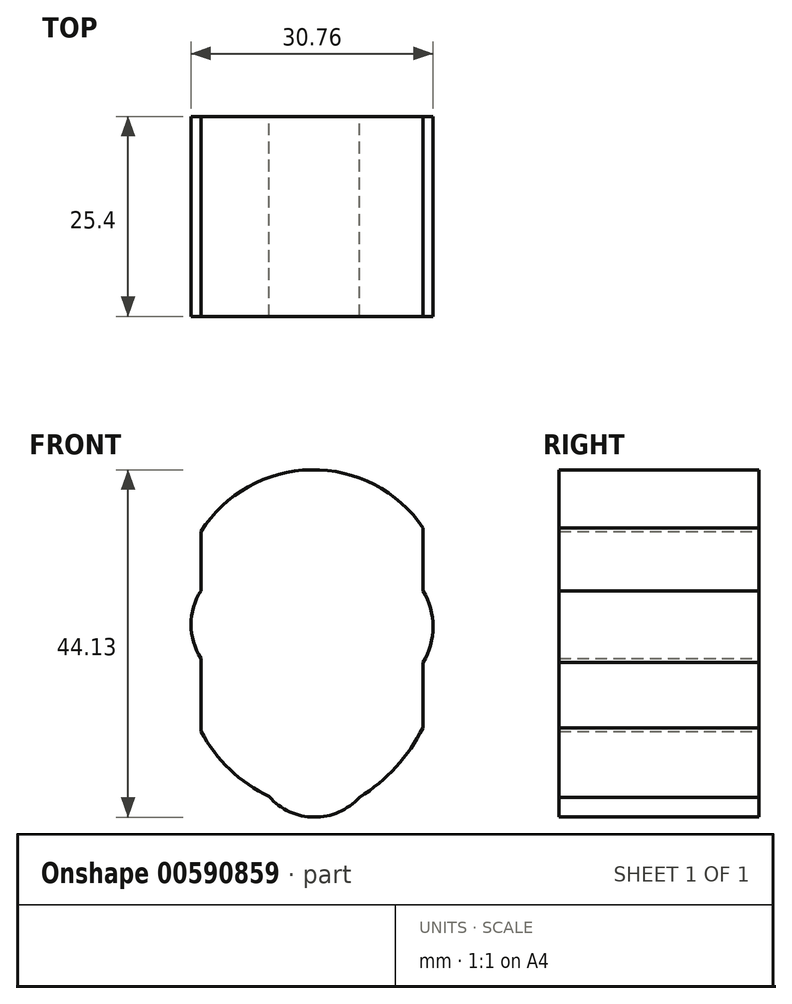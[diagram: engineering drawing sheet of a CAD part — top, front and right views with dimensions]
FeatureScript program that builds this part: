
annotation { "Feature Type Name" : "Feature", "Feature Type Description" : "" }
export const myFeature = defineFeature(function(context is Context, id is Id, definition is map)
    precondition{}
    {
        {
            var Q0;
            Q0=qCreatedBy(makeId("Front.planeOp"),FACE);
            var sketch = newSketch(context, id + "F0", { "sketchPlane" : qUnion([Q0])});
            skLineSegment(sketch, "E0", {"start": v(13.6, -3.36) * mm, "end": v(13.6, 22.02) * mm});
            skLineSegment(sketch, "E1", {"start": v(-14.59, -3.82) * mm, "end": v(-14.59, 21.56) * mm});
            skArc(sketch, "E2", {"start": v(-5.93, -12.12) * mm, "mid": v(-0.23, -14.73) * mm, "end": v(5.52, -12.22) * mm});
            skArc(sketch, "E3", {"start": v(13.6, 22.02) * mm, "mid": v(-0.62, 29.4) * mm, "end": v(-14.59, 21.56) * mm});
            skCircle(sketch, "E4", {"center": v(-5.93, 12.53) * mm, "radius": 2.55 * mm});
            skCircle(sketch, "E5", {"center": v(5.24, 12.54) * mm, "radius": 2.55 * mm});
            skArc(sketch, "E6", {"start": v(5.52, -12.22) * mm, "mid": v(10.17, -8.35) * mm, "end": v(13.6, -3.36) * mm});
            skArc(sketch, "E7", {"start": v(-14.59, -3.82) * mm, "mid": v(-10.94, -8.68) * mm, "end": v(-5.93, -12.12) * mm});
            skArc(sketch, "E8", {"start": v(-2.04, 13.98) * mm, "mid": v(-5.68, 15.47) * mm, "end": v(-9.15, 13.62) * mm});
            skArc(sketch, "E9", {"start": v(9.14, 14.07) * mm, "mid": v(5.57, 15.48) * mm, "end": v(2.03, 13.98) * mm});
            skArc(sketch, "E10", {"start": v(-4.43, -5.42) * mm, "mid": v(-0.16, -7.04) * mm, "end": v(4.1, -5.42) * mm});
            skArc(sketch, "E11", {"start": v(4.1, -5.42) * mm, "mid": v(-0.16, -4.74) * mm, "end": v(-4.43, -5.42) * mm});
            skLineSegment(sketch, "E12", {"start": v(0, 8.55) * mm, "end": v(-1.18, 3.65) * mm});
            skLineSegment(sketch, "E13", {"start": v(0, 8.55) * mm, "end": v(0.99, 3.65) * mm});
            skArc(sketch, "E14", {"start": v(-1.18, 3.65) * mm, "mid": v(-0.1, 3.45) * mm, "end": v(0.99, 3.65) * mm});
            skLineSegment(sketch, "E15", {"start": v(-0.8, -12.44) * mm, "end": v(1.7, -12.44) * mm});
            skLineSegment(sketch, "E16", {"start": v(1.7, -12.44) * mm, "end": v(0.92, -14.65) * mm});
            skLineSegment(sketch, "E17", {"start": v(0.92, -14.65) * mm, "end": v(-0.88, -14.7) * mm});
            skLineSegment(sketch, "E18", {"start": v(-0.88, -14.7) * mm, "end": v(-1.52, -12.44) * mm});
            skLineSegment(sketch, "E19", {"start": v(-1.52, -12.44) * mm, "end": v(-0.8, -12.44) * mm});
            skArc(sketch, "E20", {"start": v(5.21, -5.2) * mm, "mid": v(-0.15, -4.35) * mm, "end": v(-5.55, -5) * mm});
            skArc(sketch, "E21", {"start": v(5.21, -5.2) * mm, "mid": v(-0.14, -3.37) * mm, "end": v(-5.55, -5) * mm});
            skArc(sketch, "E22", {"start": v(-14.59, 21.56) * mm, "mid": v(-6.77, 23.99) * mm, "end": v(-0.62, 29.4) * mm});
            skArc(sketch, "E23", {"start": v(-14.59, 21.56) * mm, "mid": v(-8.02, 24.5) * mm, "end": v(-2.63, 29.24) * mm});
            skArc(sketch, "E24", {"start": v(-13.44, 23.16) * mm, "mid": v(-9, 25.5) * mm, "end": v(-5.15, 28.7) * mm});
            skArc(sketch, "E25", {"start": v(2.47, 29.16) * mm, "mid": v(7, 23.99) * mm, "end": v(13.6, 22.02) * mm});
            skArc(sketch, "E26", {"start": v(2.47, 29.16) * mm, "mid": v(7.52, 24.79) * mm, "end": v(13.6, 22.02) * mm});
            skArc(sketch, "E27", {"start": v(13.6, 22.02) * mm, "mid": v(8.05, 25.62) * mm, "end": v(2.47, 29.16) * mm});
            skArc(sketch, "E28", {"start": v(-14.59, 14.03) * mm, "mid": v(-15.86, 9.74) * mm, "end": v(-14.59, 5.45) * mm});
            skArc(sketch, "E29", {"start": v(13.6, 4.9) * mm, "mid": v(14.9, 9.47) * mm, "end": v(13.6, 14.03) * mm});
            skSolve(sketch);
        }
        {
            var Q0;
            Q0=makeQuery(id+"F0.imprint","IMPRINT",FACE,{"disambiguationData":[TD([[makeQuery(id+"F0.imprint","IMPRINT",EDGE,{"derivedFrom":sQuery(id+"F0.wireOp",EDGE,"E25")}),1.0]])]});
            var Q1;
            Q1=makeQuery(id+"F0.imprint","IMPRINT",FACE,{"disambiguationData":[TD([[makeQuery(id+"F0.imprint","IMPRINT",EDGE,{"derivedFrom":sQuery(id+"F0.wireOp",EDGE,"E26")}),1.0]])]});
            var Q2;
            {var subQ0=sQuery(id+"F0.wireOp",EDGE,"E27");Q2=makeQuery(id+"F0.imprint","IMPRINT",FACE,{"disambiguationData":[TD([[makeQuery(id+"F0.imprint","IMPRINT",EDGE,{"derivedFrom":subQ0}),-1.0]])]});}
            var Q3;
            Q3=makeQuery(id+"F0.imprint","IMPRINT",FACE,{"disambiguationData":[TD([[makeQuery(id+"F0.imprint","IMPRINT",EDGE,{"derivedFrom":sQuery(id+"F0.wireOp",EDGE,"E4")}),1.0]])]});
            var Q4;
            Q4=makeQuery(id+"F0.imprint","IMPRINT",FACE,{"disambiguationData":[TD([[makeQuery(id+"F0.imprint","IMPRINT",EDGE,{"derivedFrom":sQuery(id+"F0.wireOp",EDGE,"E5")}),1.0]])]});
            var Q5;
            Q5=makeQuery(id+"F0.imprint","IMPRINT",FACE,{"disambiguationData":[TD([[makeQuery(id+"F0.imprint","IMPRINT",EDGE,{"derivedFrom":sQuery(id+"F0.wireOp",EDGE,"E10")}),1.0]])]});
            var Q6;
            Q6=makeQuery(id+"F0.imprint","IMPRINT",FACE,{"disambiguationData":[TD([[makeQuery(id+"F0.imprint","IMPRINT",EDGE,{"derivedFrom":sQuery(id+"F0.wireOp",EDGE,"E20")}),-1.0]])]});
            var Q7;
            {var subQ0=sQuery(id+"F0.wireOp",EDGE,"E29");Q7=makeQuery(id+"F0.imprint","IMPRINT",FACE,{"disambiguationData":[TD([[makeQuery(id+"F0.imprint","IMPRINT",EDGE,{"derivedFrom":subQ0}),1.0]])]});}
            var Q8;
            Q8=makeQuery(id+"F0.imprint","IMPRINT",FACE,{"disambiguationData":[TD([[makeQuery(id+"F0.imprint","IMPRINT",EDGE,{"derivedFrom":sQuery(id+"F0.wireOp",EDGE,"E12")}),1.0]])]});
            var Q9;
            Q9=makeQuery(id+"F0.imprint","IMPRINT",FACE,{"disambiguationData":[TD([[makeQuery(id+"F0.imprint","IMPRINT",EDGE,{"derivedFrom":sQuery(id+"F0.wireOp",EDGE,"E4")}),-1.0]])]});
            var Q10;
            {var subQ0=sQuery(id+"F0.wireOp",EDGE,"E28");Q10=makeQuery(id+"F0.imprint","IMPRINT",FACE,{"disambiguationData":[TD([[makeQuery(id+"F0.imprint","IMPRINT",EDGE,{"derivedFrom":subQ0}),1.0]])]});}
            var Q11;
            {var subQ0=sQuery(id+"F0.wireOp",EDGE,"E24");Q11=makeQuery(id+"F0.imprint","IMPRINT",FACE,{"disambiguationData":[TD([[makeQuery(id+"F0.imprint","IMPRINT",EDGE,{"derivedFrom":subQ0}),1.0]])]});}
            var Q12;
            {var subQ0=sQuery(id+"F0.wireOp",EDGE,"E22");Q12=makeQuery(id+"F0.imprint","IMPRINT",FACE,{"disambiguationData":[TD([[makeQuery(id+"F0.imprint","IMPRINT",EDGE,{"derivedFrom":subQ0}),1.0]])]});}
            var Q13;
            {var subQ0=sQuery(id+"F0.wireOp",EDGE,"E23");Q13=makeQuery(id+"F0.imprint","IMPRINT",FACE,{"disambiguationData":[TD([[makeQuery(id+"F0.imprint","IMPRINT",EDGE,{"derivedFrom":subQ0}),1.0]])]});}
            var Q14;
            Q14=makeQuery(id+"F0.imprint","IMPRINT",FACE,{"disambiguationData":[TD([[makeQuery(id+"F0.imprint","IMPRINT",EDGE,{"derivedFrom":sQuery(id+"F0.wireOp",EDGE,"E15")}),-1.0]])]});
            var Q15;
            {var subQ0=sQuery(id+"F0.wireOp",EDGE,"E17");Q15=makeQuery(id+"F0.imprint","IMPRINT",FACE,{"disambiguationData":[TD([[makeQuery(id+"F0.imprint","IMPRINT",EDGE,{"derivedFrom":subQ0}),1.0]])]});}
            extrude(context, id + "F1", {"entities" : qUnion([Q0, Q1, Q2, Q3, Q4, Q5, Q6, Q7, Q8, Q9, Q10, Q11, Q12, Q13, Q14, Q15]), "depth" : 25.4 * mm, "offsetDistance" : 25.4 * mm});
        }
    });
